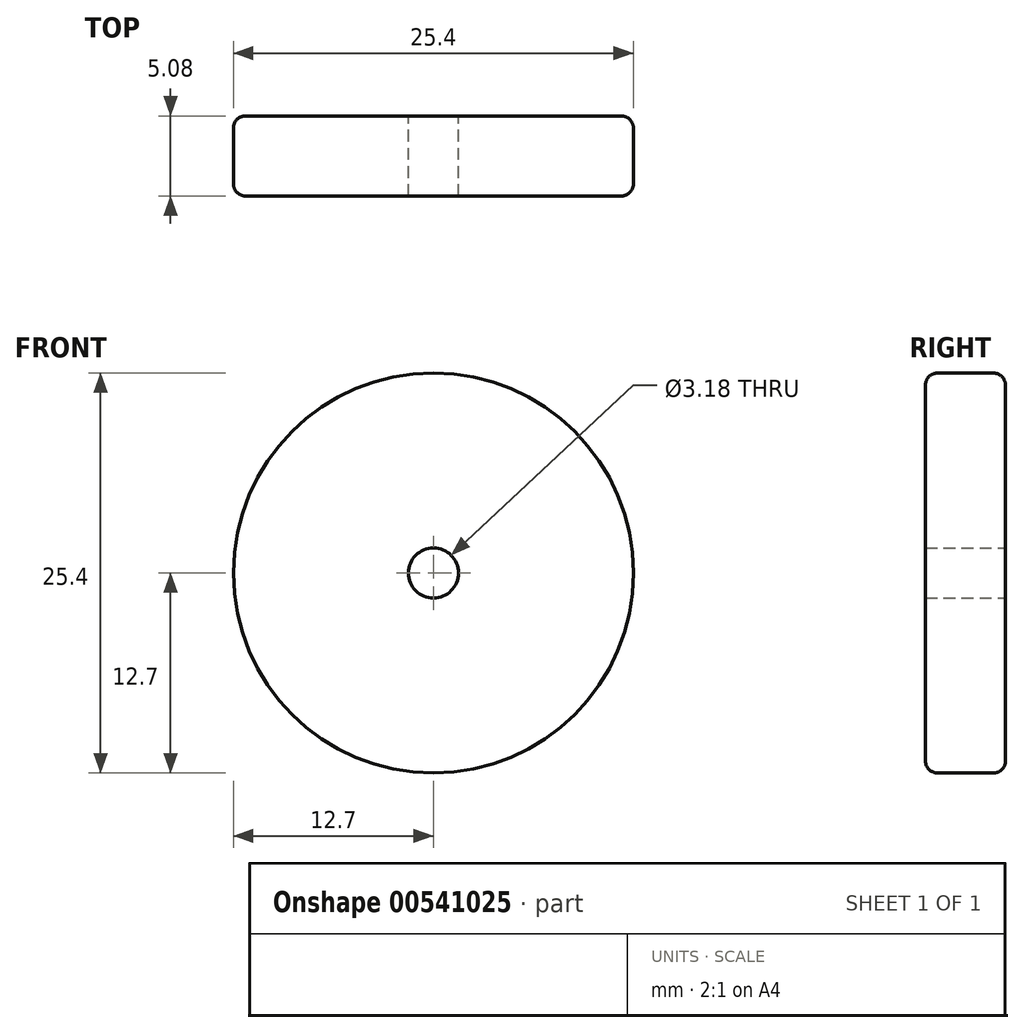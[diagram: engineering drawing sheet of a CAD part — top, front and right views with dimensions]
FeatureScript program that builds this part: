
annotation { "Feature Type Name" : "Feature", "Feature Type Description" : "" }
export const myFeature = defineFeature(function(context is Context, id is Id, definition is map)
    precondition{}
    {
        {
            var Q0;
            Q0=qCreatedBy(makeId("Front.planeOp"),FACE);
            var sketch = newSketch(context, id + "F0", { "sketchPlane" : qUnion([Q0])});
            skCircle(sketch, "E0", {"center": v(0, 0) * mm, "radius": 12.7 * mm});
            skCircle(sketch, "E1", {"center": v(0, 0) * mm, "radius": 1.59 * mm});
            skSolve(sketch);
        }
        {
            var Q0;
            Q0=makeQuery(id+"F0.imprint","IMPRINT",FACE,{"disambiguationData":[TD([[makeQuery(id+"F0.imprint","IMPRINT",EDGE,{"derivedFrom":sQuery(id+"F0.wireOp",EDGE,"E0")}),1.0]])]});
            extrude(context, id + "F1", {"entities" : qUnion([Q0]), "depth" : 5.08 * mm, "offsetDistance" : 25.4 * mm});
        }
        {
            var Q0;
            Q0=makeQuery(id+"F1.opExtrude","CAP_EDGE",EDGE,{"disambiguationData":[OSD([sQuery(id+"F0.wireOp",EDGE,"E0")])],"isStart":true});
            var Q1;
            Q1=makeQuery(id+"F1.opExtrude","CAP_EDGE",EDGE,{"disambiguationData":[OSD([sQuery(id+"F0.wireOp",EDGE,"E0")])],"isStart":false});
            fillet(context, id + "F2", {"entities" : qUnion([Q0, Q1]), "radius" : 0.76 * mm, "tangentPropagation" : true, "allowEdgeOverflow" : false});
        }
    });
